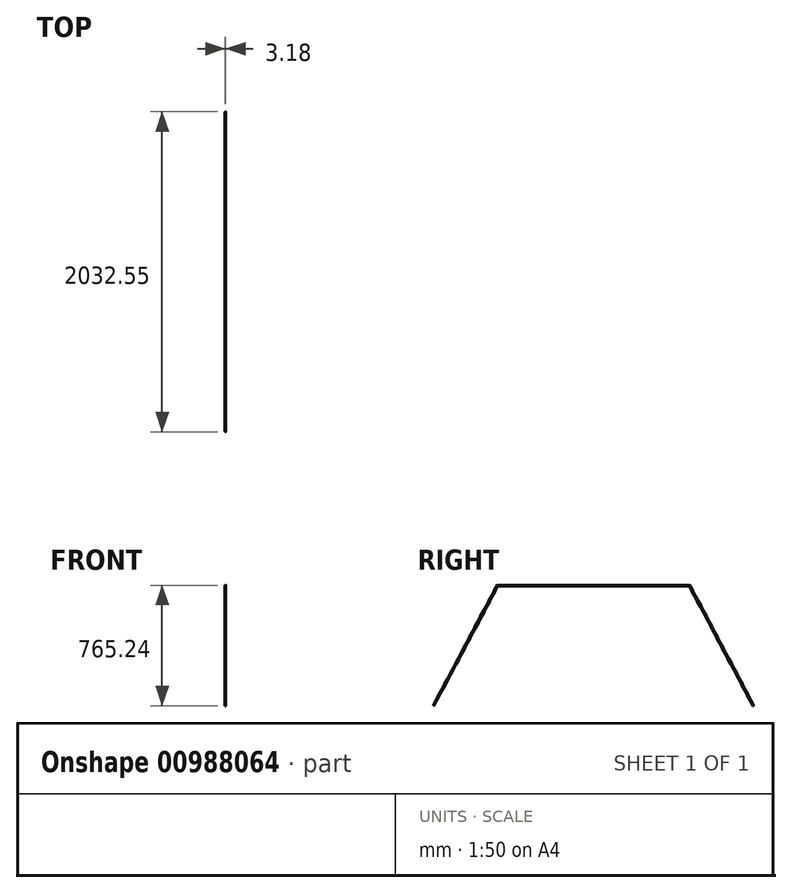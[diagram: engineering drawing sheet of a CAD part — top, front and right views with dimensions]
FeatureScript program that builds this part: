
annotation { "Feature Type Name" : "Feature", "Feature Type Description" : "" }
export const myFeature = defineFeature(function(context is Context, id is Id, definition is map)
    precondition{}
    {
        {
            var Q0;
            Q0=qCreatedBy(makeId("Right.planeOp"),FACE);
            var sketch = newSketch(context, id + "F0", { "sketchPlane" : qUnion([Q0])});
            skLineSegment(sketch, "E0", {"start": v(0, 0) * mm, "end": v(405.44, 762.51) * mm});
            skLineSegment(sketch, "E1", {"start": v(405.44, 762.51) * mm, "end": v(1624.64, 762.51) * mm});
            skLineSegment(sketch, "E2", {"start": v(1624.64, 762.51) * mm, "end": v(2030.07, 0) * mm});
            skSolve(sketch);
        }
        {
            var Q0;
            Q0=qCreatedBy(makeId("Top.planeOp"),FACE);
            var sketch = newSketch(context, id + "F1", { "sketchPlane" : qUnion([Q0])});
            skCircle(sketch, "E3", {"center": v(0, 0) * mm, "radius": 1.59 * mm});
            skSolve(sketch);
        }
        {
            var Q0;
            Q0=makeQuery(id+"F1.imprint","IMPRINT",FACE,{"disambiguationData":[TD([[makeQuery(id+"F1.imprint","IMPRINT",EDGE,{"derivedFrom":sQuery(id+"F1.wireOp",EDGE,"E3")}),1.0]])]});
            var Q1;
            Q1=sQuery(id+"F0.wireOp",EDGE,"E0");
            var Q2;
            Q2=sQuery(id+"F0.wireOp",EDGE,"E1");
            var Q3;
            Q3=sQuery(id+"F0.wireOp",EDGE,"E2");
            sweep(context, id + "F2", {"profiles" : qUnion([Q0]), "path" : qUnion([Q1, Q2, Q3])});
        }
    });
